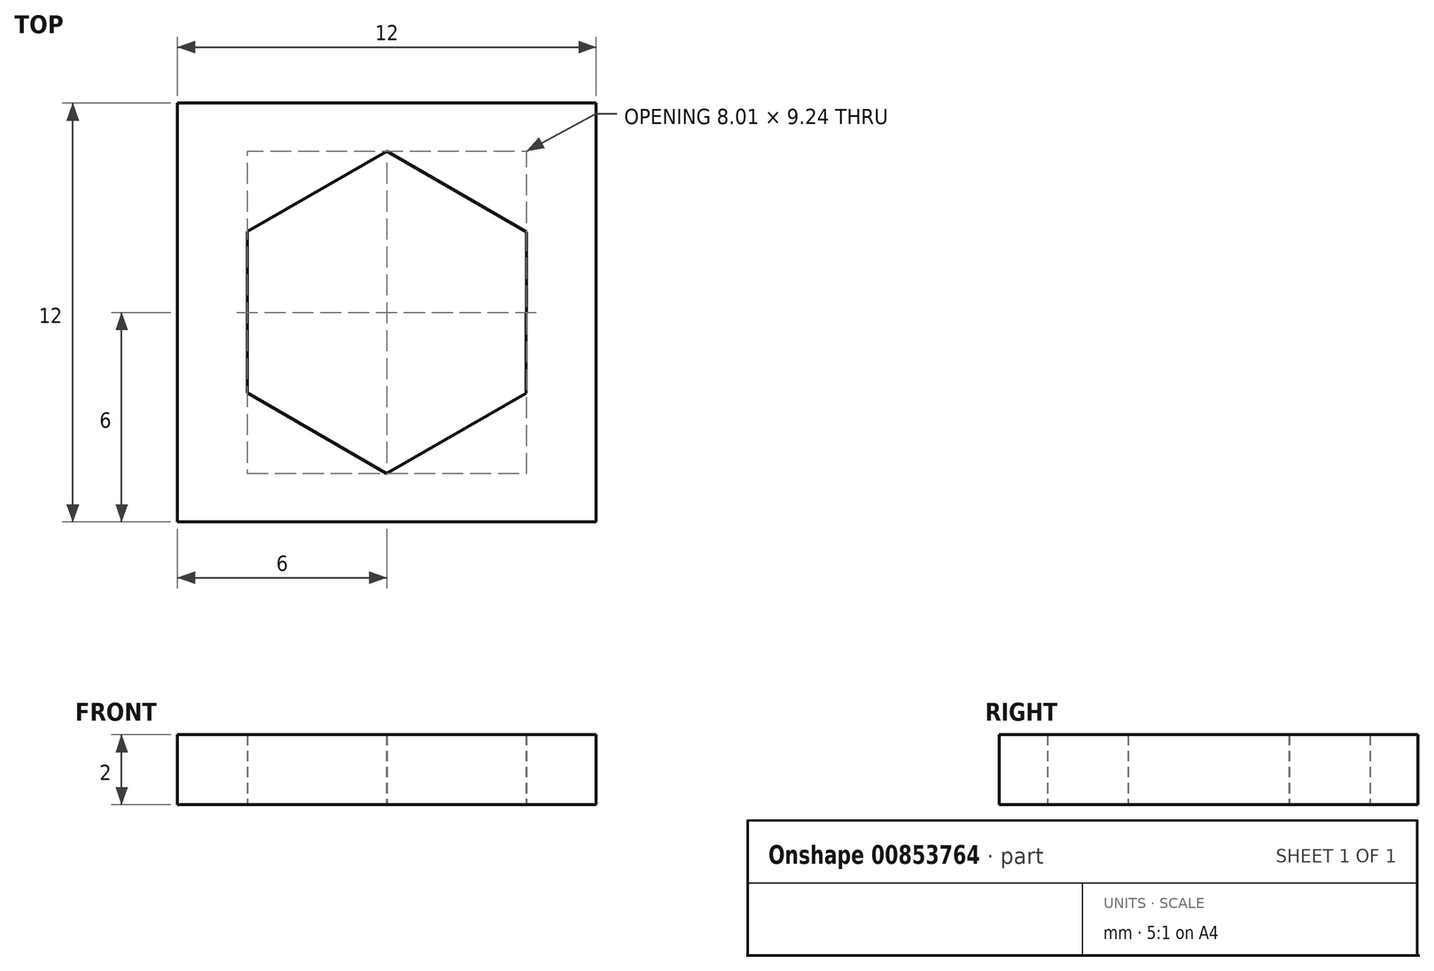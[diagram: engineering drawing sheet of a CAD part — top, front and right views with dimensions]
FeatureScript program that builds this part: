
annotation { "Feature Type Name" : "Feature", "Feature Type Description" : "" }
export const myFeature = defineFeature(function(context is Context, id is Id, definition is map)
    precondition{}
    {
        {
            var Q0;
            Q0=qCreatedBy(makeId("Top.planeOp"),FACE);
            var sketch = newSketch(context, id + "F0", { "sketchPlane" : qUnion([Q0])});
            skLineSegment(sketch, "E0.bottom", {"start": v(6, -6) * mm, "end": v(-6, -6) * mm});
            skLineSegment(sketch, "E0.top", {"start": v(6, 6) * mm, "end": v(-6, 6) * mm});
            skLineSegment(sketch, "E0.left", {"start": v(6, -6) * mm, "end": v(6, 6) * mm});
            skLineSegment(sketch, "E0.right", {"start": v(-6, -6) * mm, "end": v(-6, 6) * mm});
            skPoint(sketch, "E0.middle", {"position": v(0, 0) * mm});
            skCircle(sketch, "E1.cCircle", {"center": v(0, 0) * mm, "radius": 4 * mm, "construction": true});
            skLineSegment(sketch, "E1.0", {"start": v(4, -2.31) * mm, "end": v(0, -4.62) * mm});
            skLineSegment(sketch, "E1.1", {"start": v(0, -4.62) * mm, "end": v(-4, -2.3) * mm});
            skLineSegment(sketch, "E1.2", {"start": v(-4, -2.3) * mm, "end": v(-4, 2.31) * mm});
            skLineSegment(sketch, "E1.3", {"start": v(-4, 2.31) * mm, "end": v(0, 4.62) * mm});
            skLineSegment(sketch, "E1.4", {"start": v(0, 4.62) * mm, "end": v(4, 2.3) * mm});
            skLineSegment(sketch, "E1.5", {"start": v(4, 2.3) * mm, "end": v(4, -2.31) * mm});
            skPoint(sketch, "E1.0.midPoint", {"position": v(2, -3.47) * mm});
            skSolve(sketch);
        }
        {
            var Q0;
            Q0=makeQuery(id+"F0.imprint","IMPRINT",FACE,{"disambiguationData":[TD([[makeQuery(id+"F0.imprint","IMPRINT",EDGE,{"derivedFrom":sQuery(id+"F0.wireOp",EDGE,"E0.bottom")}),-1.0]])]});
            extrude(context, id + "F1", {"entities" : qUnion([Q0]), "depth" : 2 * mm, "offsetDistance" : 25 * mm});
        }
    });
